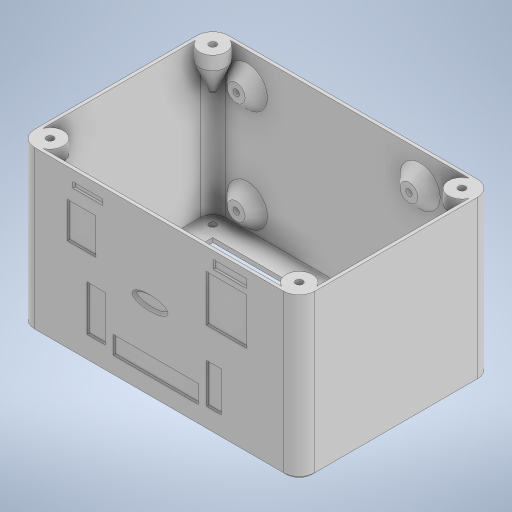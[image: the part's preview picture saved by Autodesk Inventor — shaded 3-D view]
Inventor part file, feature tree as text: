
AUTODESK INVENTOR PART (.ipt)
format: ipt  version: 2023 (Build 270158030, 158C)  size: 1,020,416 bytes
history: native  units: mm
features: sketch x23, extrude x21, projected_geometry x16, chamfer x7, other x5, fillet x4, mirror x3, plane x1, loft x1, pattern_circular x1, revolve x1
ambient origin geometry x8: Origin, YZ Plane, XZ Plane, XY Plane, X Axis, Y Axis, Z Axis, Center Point
bodies: Body1 (feature_tree), Body2 (feature_tree), Body3 (feature_tree), Body4 (feature_tree)
feature tree (83):
  other  "base-plate"
  extrude  "Extrusion1"  Depth=83.0mm
  extrude  "Extrusion2"  Depth=3.5mm
  fillet  "Fillet1"  Radius=3.5mm
  extrude  "Extrusion3"  Depth=5.0mm
  extrude  "Extrusion4"  Depth=5.0mm
  extrude  "Extrusion6"  TaperAngle=0.0deg  [1 undecoded]
  extrude  "Extrusion7"  Depth=10.0mm
  chamfer  "Chamfer1"  Distance=2.0mm
  extrude  "Extrusion8"  Depth=1.5mm TaperAngle=0.0deg
  chamfer  "Chamfer2"  Distance=1.0mm
  chamfer  "Chamfer3"  Distance=5.0mm
  extrude  "Extrusion9"  Depth=2.0mm
  plane  "Work Plane1"
  sketch  "Sketch11"  dims[d23=8.0mm]
  loft  "Loft1"
  chamfer  "Chamfer4"  Distance=1.5mm Angle=45.0deg
  pattern_circular  "Circular Pattern1"  Count=2 Angle=360.0deg
  mirror  "Mirror1"
  chamfer  "Chamfer5"  Distance=2.0mm Angle=45.0deg
  extrude  "Extrusion10"  Depth=1.5mm TaperAngle=0.0deg
  extrude  "Extrusion11"  Depth=8.0mm
  chamfer  "Chamfer6"  Distance=8.0mm
  extrude  "Extrusion12"  Depth=5.0mm
  chamfer  "Chamfer7"  Distance=10.0mm
  fillet  "Fillet2"  [1 undecoded]
  extrude  "Extrusion13"  Depth=2.0mm
  extrude  "Extrusion14"  Depth=10.0mm TaperAngle=0.0deg
  extrude  "Extrusion15"  Depth=3.0mm TaperAngle=0.0deg
  extrude  "Extrusion16"  Depth=24.0mm
  extrude  "Extrusion17"  TaperAngle=0.0deg  [1 undecoded]
  extrude  "Extrusion18"  Depth=24.0mm
  fillet  "Fillet3"  Radius=15.0mm
  revolve  "Revolution1"  [1 undecoded]
  extrude  "Extrusion19"  Depth=0.4mm
  extrude  "Extrusion20"  Depth=0.4mm
  sketch  "Sketch26"  dims[d67=3.0mm d68=2.0mm d69=45.0deg d70=30.0mm d71=8.0mm d72=0.0mm]
  extrude  "Extrusion21"  Depth=0.4mm
  fillet  "Fillet4"  [1 undecoded]
  mirror  "Mirror2"
  mirror  "Mirror3"
  extrude  "Extrusion22"  TaperAngle=0.0deg  [1 undecoded]
  sketch  "Sketch1"  dims[d0=121.75mm d1=83.0mm]
  sketch  "Sketch2"  dims[d2=60.875mm d3=41.5mm d4=3.5mm d5=0.0mm]
  sketch  "Sketch3"  dims[d6=3.2mm d7=5.0mm]
  projected_geometry  "Projected Loop1"
  other  "head"
  sketch  "Sketch4"  dims[d8=5.0mm d9=5.0mm]
  projected_geometry  "Projected Loop2"
  sketch  "Sketch5"  dims[d10=5.0mm d11=0.0mm d12=0.0mm]
  sketch  "Sketch6"  dims[d13=5.0mm d14=10.0mm]
  sketch  "Sketch7"  dims[d15=2.0mm d16=2.0mm d17=0.0mm]
  projected_geometry  "Projected Loop3"
  projected_geometry  "Projected Loop4"
  projected_geometry  "Projected Loop5"
  projected_geometry  "Projected Loop6"
  sketch  "Sketch9"  dims[d18=1.5mm d19=70.0mm d20=0.0mm]
  projected_geometry  "Projected Loop7"
  projected_geometry  "Projected Loop8"
  projected_geometry  "Projected Loop9"
  projected_geometry  "Projected Loop10"
  sketch  "Sketch13"  dims[d24=46.0mm d26=1.0mm d27=0.0mm]
  projected_geometry  "Projected Loop11"
  other  "lid"
  sketch  "Sketch14"  dims[d28=10.0mm]
  projected_geometry  "Projected Loop12"
  sketch  "Sketch15"  dims[d29=77.5mm]
  sketch  "Sketch16"  dims[d30=10.0mm d31=5.0mm d32=0.0mm]
  sketch  "Sketch17"  dims[d33=5.0mm d34=2.0mm d35=45.0deg d36=2.9mm]
  projected_geometry  "Projected Loop13"
  other  "antenna"
  sketch  "Sketch18"  dims[d37=8.0mm d38=0.0mm d39=1.0mm d40=2.0mm d41=45.0deg d42=1.5mm d43=2.0mm d44=45.0deg]
  sketch  "Sketch19"  dims[d45=12.0mm]
  projected_geometry  "Projected Loop14"
  sketch  "Sketch20"  dims[d46=6.0mm d47=0.0mm]
  sketch  "Sketch21"  dims[d48=15.0mm]
  sketch  "Sketch23"  dims[d49=3.0mm]
  sketch  "Sketch24"  dims[d50=0.0mm d51=90.0deg d52=0.0mm d53=90.0deg d54=1.49mm d55=2.0mm d56=45.0deg d57=20.0mm d58=360.0deg d60=1.49mm d61=2.0mm d62=45.0deg]
  projected_geometry  "Projected Loop15"
  sketch  "Sketch25"  dims[d63=2.0mm d64=0.0mm d65=1.5mm d66=0.0mm]
  other  "Edges1"
  sketch  "Sketch27"  dims[d73=6.0mm d74=2.0mm d75=45.0deg d76=5.0mm d77=10.0mm d78=0.0mm d79=0.0mm d80=2.0mm d81=10.0mm d82=0.0mm d83=3.0mm d84=0.0mm d85=42.0mm d86=-0.349066mm d87=0.0mm d88=0.0mm d89=20.0mm d90=15.0mm d91=0.0mm d92=8.0mm d93=0.4mm d94=0.4mm d95=0.4mm d96=90.0deg d97=0.0mm d98=0.0mm d99=3.0mm d100=6.0mm d101=12.0mm d102=26.5mm d103=33.5mm d104=20.0mm d105=4.5mm d106=40.0mm d107=28.5mm d108=9.5mm d109=36.0mm d110=27.0mm d111=41.0mm d112=29.5mm d113=0.0mm d114=0.0mm d115=18.0mm d116=6.3mm d117=13.25mm d118=7.2mm d119=10.0mm d120=0.0mm d121=2.0mm d122=3.0mm d123=3.0mm d124=24.0mm d125=24.0mm d126=0.0mm d127=0.0mm]
  projected_geometry  "Projected Loop16"
note: 6 required parameter values undecoded (feature->parameter linkage not recoverable at this tier; creation-order binding heuristic only, values carry confidence <= 0.55)